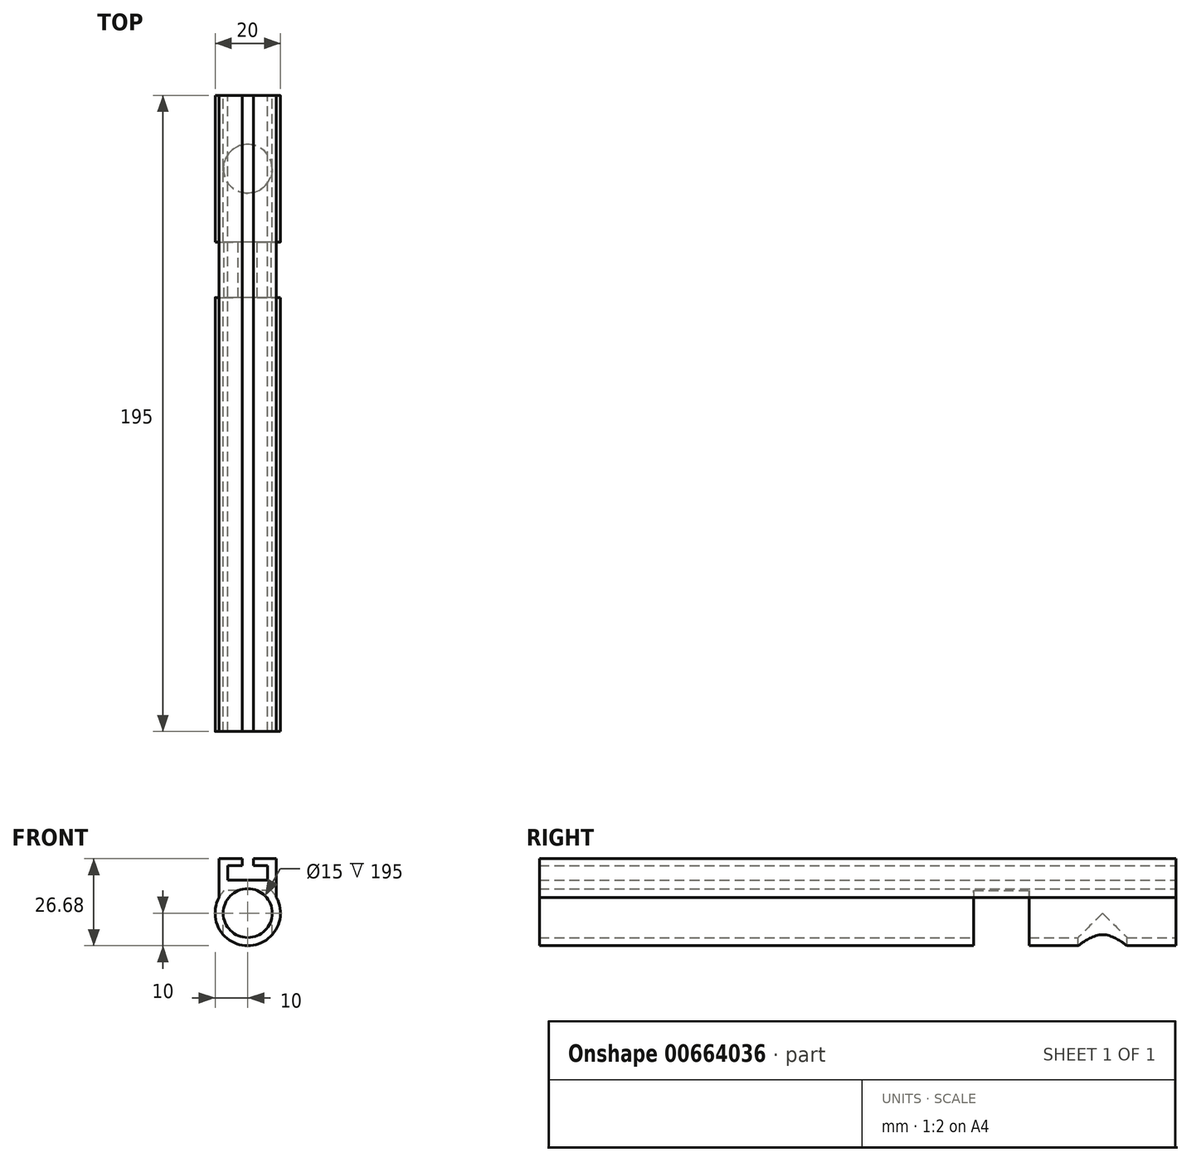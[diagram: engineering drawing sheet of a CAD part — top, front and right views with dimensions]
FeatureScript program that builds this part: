
annotation { "Feature Type Name" : "Feature", "Feature Type Description" : "" }
export const myFeature = defineFeature(function(context is Context, id is Id, definition is map)
    precondition{}
    {
        {
            var Q0;
            Q0=qCreatedBy(makeId("Front.planeOp"),FACE);
            var sketch = newSketch(context, id + "F0", { "sketchPlane" : qUnion([Q0])});
            skCircle(sketch, "E0", {"center": v(0, 0) * mm, "radius": 7.5 * mm});
            skCircle(sketch, "E1", {"center": v(0, 0) * mm, "radius": 10 * mm});
            skSolve(sketch);
        }
        {
            var Q0;
            Q0=makeQuery(id+"F0.imprint","IMPRINT",FACE,{"disambiguationData":[TD([[makeQuery(id+"F0.imprint","IMPRINT",EDGE,{"derivedFrom":sQuery(id+"F0.wireOp",EDGE,"E0")}),-1.0]])]});
            extrude(context, id + "F1", {"entities" : qUnion([Q0]), "depth" : 195 * mm, "offsetDistance" : 25 * mm});
        }
        {
            var Q0;
            Q0=qCreatedBy(makeId("Top.planeOp"),FACE);
            var sketch = newSketch(context, id + "F2", { "sketchPlane" : qUnion([Q0])});
            skCircle(sketch, "E2", {"center": v(0, -22.5) * mm, "radius": 7.5 * mm});
            skSolve(sketch);
        }
        {
            var Q0;
            Q0 = qSketchRegion(id + "F2", true);
            extrude(context, id + "F3", {"entities" : qUnion([Q0]), "operationType" : NewBodyOperationType.REMOVE, "oppositeDirection" : true, "depth" : 25 * mm, "offsetDistance" : 25 * mm});
        }
        {
            var Q0;
            Q0=qCreatedBy(makeId("Top.planeOp"),FACE);
            var sketch = newSketch(context, id + "F4", { "sketchPlane" : qUnion([Q0])});
            skLineSegment(sketch, "E3.bottom", {"start": v(12.93, -62) * mm, "end": v(-12.93, -62) * mm});
            skLineSegment(sketch, "E3.top", {"start": v(12.93, -45) * mm, "end": v(-12.93, -45) * mm});
            skLineSegment(sketch, "E3.left", {"start": v(12.93, -62) * mm, "end": v(12.93, -45) * mm});
            skLineSegment(sketch, "E3.right", {"start": v(-12.93, -62) * mm, "end": v(-12.93, -45) * mm});
            skPoint(sketch, "E3.middle", {"position": v(0, -53.5) * mm});
            skSolve(sketch);
        }
        {
            var Q0;
            Q0 = qSketchRegion(id + "F4", true);
            extrude(context, id + "F5", {"entities" : qUnion([Q0]), "operationType" : NewBodyOperationType.REMOVE, "oppositeDirection" : true, "depth" : 25 * mm, "offsetDistance" : 25 * mm});
        }
        {
            var Q0;
            Q0 = qSketchRegion(id + "F4", true);
            extrude(context, id + "F6", {"entities" : qUnion([Q0]), "operationType" : NewBodyOperationType.REMOVE, "depth" : 6.9 * mm, "offsetDistance" : 25 * mm});
        }
        {
            var Q0;
            Q0=qCreatedBy(makeId("Front.planeOp"),FACE);
            var sketch = newSketch(context, id + "F7", { "sketchPlane" : qUnion([Q0])});
            skCircle(sketch, "E4.0", {"center": v(0, 0) * mm, "radius": 10 * mm});
            skLineSegment(sketch, "E5.MirrorCS", {"start": v(8.8, 5.52) * mm, "end": v(8.8, 16.68) * mm});
            skLineSegment(sketch, "E6.MirrorCS", {"start": v(8.8, 16.68) * mm, "end": v(1.73, 16.68) * mm});
            skLineSegment(sketch, "E7.MirrorCS", {"start": v(1.73, 14.57) * mm, "end": v(6.1, 14.57) * mm});
            skLineSegment(sketch, "E8.MirrorCS", {"start": v(6.1, 14.57) * mm, "end": v(6.1, 10.12) * mm});
            skLineSegment(sketch, "E9.MirrorCS", {"start": v(1.73, 16.68) * mm, "end": v(1.73, 14.57) * mm});
            skLineSegment(sketch, "E10.MirrorCS", {"start": v(-8.8, 16.68) * mm, "end": v(-1.73, 16.68) * mm});
            skLineSegment(sketch, "E11.MirrorCS", {"start": v(-1.73, 16.68) * mm, "end": v(-1.73, 14.57) * mm});
            skLineSegment(sketch, "E12.MirrorCS", {"start": v(-1.73, 14.57) * mm, "end": v(-6.1, 14.57) * mm});
            skLineSegment(sketch, "E13.MirrorCS", {"start": v(-8.8, 5.52) * mm, "end": v(-8.8, 16.68) * mm});
            skLineSegment(sketch, "E14.MirrorCS", {"start": v(-6.1, 14.57) * mm, "end": v(-6.1, 10.12) * mm});
            skLineSegment(sketch, "E15", {"start": v(-6.1, 10.12) * mm, "end": v(-6.1, 7.77) * mm});
            skLineSegment(sketch, "E16", {"start": v(-8.8, 5.52) * mm, "end": v(-8.8, 4.76) * mm});
            skLineSegment(sketch, "E17", {"start": v(8.8, 5.52) * mm, "end": v(8.8, 4.12) * mm});
            skLineSegment(sketch, "E18", {"start": v(6.1, 10.12) * mm, "end": v(6.1, 7.65) * mm});
            skLineSegment(sketch, "E19.bottom", {"start": v(-6.1, 14.57) * mm, "end": v(6.1, 14.57) * mm});
            skLineSegment(sketch, "E19.top", {"start": v(-6.1, 10.12) * mm, "end": v(6.1, 10.12) * mm});
            skLineSegment(sketch, "E20", {"start": v(-6.1, 7.77) * mm, "end": v(-6.1, 7.65) * mm});
            skLineSegment(sketch, "E21", {"start": v(-6.1, 7.65) * mm, "end": v(6.1, 7.65) * mm});
            skSolve(sketch);
        }
        {
            var Q0;
            Q0=makeQuery(id+"F7.imprint","IMPRINT",FACE,{"disambiguationData":[TD([[makeQuery(id+"F7.imprint","IMPRINT",EDGE,{"derivedFrom":sQuery(id+"F7.wireOp",EDGE,"E5.MirrorCS")}),1.0]])]});
            var Q1;
            Q1=makeQuery(id+"F7.imprint","IMPRINT",FACE,{"disambiguationData":[TD([[makeQuery(id+"F7.imprint","IMPRINT",EDGE,{"derivedFrom":sQuery(id+"F7.wireOp",EDGE,"E10.MirrorCS")}),-1.0]])]});
            var Q2;
            {var subQ5=sQuery(id+"F7.wireOp",EDGE,"E19.top");Q2=makeQuery(id+"F7.imprint","IMPRINT",FACE,{"disambiguationData":[TD([[makeQuery(id+"F7.imprint","IMPRINT",EDGE,{"derivedFrom":subQ5}),-1.0]])]});}
            extrude(context, id + "F8", {"entities" : qUnion([Q0, Q1, Q2]), "operationType" : NewBodyOperationType.ADD, "depth" : 195 * mm, "offsetDistance" : 25 * mm});
        }
    });
